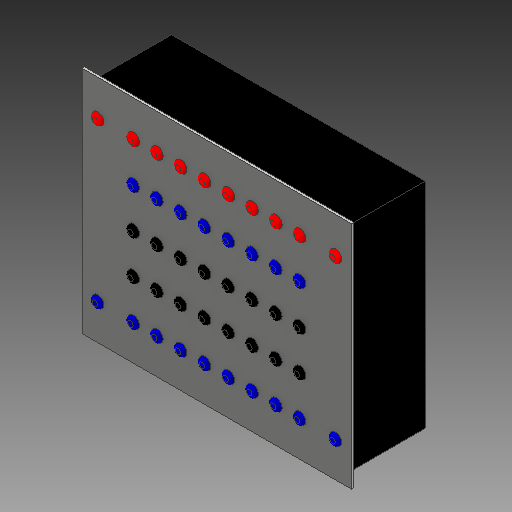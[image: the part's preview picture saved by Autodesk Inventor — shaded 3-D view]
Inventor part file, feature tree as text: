
AUTODESK INVENTOR PART (.ipt)
format: ipt  version: 2019 (Build 230136000, 136)  size: 252,928 bytes
history: native  units: mm
features: extrude x3, sketch x3, fillet x1
ambient origin geometry x8: Origin, YZ Plane, XZ Plane, XY Plane, X Axis, Y Axis, Z Axis, Center Point
bodies: Solid1 (feature_tree)
feature tree (7):
  extrude  "Extrusion1"  Depth=270.0mm
  extrude  "Extrusion2"  Depth=340.0mm
  extrude  "Extrusion3"  Depth=10.0mm
  fillet  "Fillet1"  Radius=10.0mm
  sketch  "Sketch1"  dims[d0=320.0mm d1=270.0mm]
  sketch  "Sketch2"  dims[d2=100.0mm d3=0.0mm d4=340.0mm]
  sketch  "Sketch3"  dims[d5=290.0mm d6=10.0mm d7=10.0mm d8=3.0mm d9=0.0mm d11=15.0mm d12=265.0mm d13=85.0mm d14=135.0mm d16=185.0mm d17=235.0mm d18=35.0mm d19=310.0mm d20=80.0mm d22=30.0mm d23=10.0mm d25=10.0mm d27=10.0mm d28=4.0mm d29=0.0mm d30=4.0mm]
